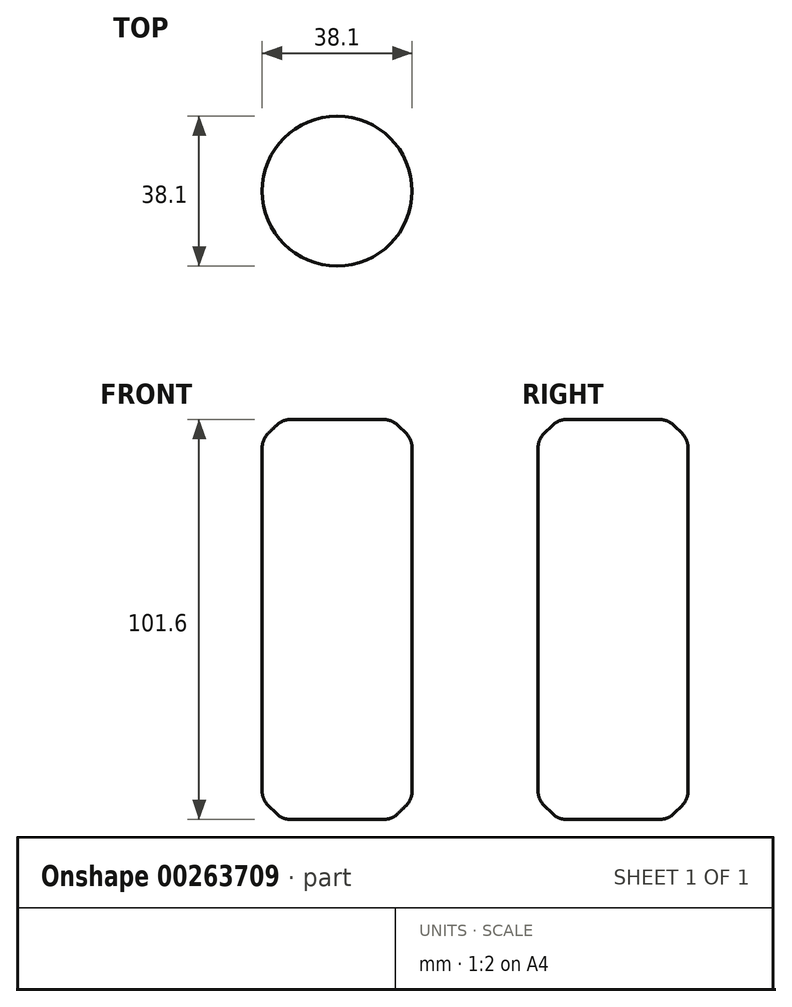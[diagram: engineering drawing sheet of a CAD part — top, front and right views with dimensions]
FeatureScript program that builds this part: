
annotation { "Feature Type Name" : "Feature", "Feature Type Description" : "" }
export const myFeature = defineFeature(function(context is Context, id is Id, definition is map)
    precondition{}
    {
        {
            var Q0;
            Q0=qCreatedBy(makeId("Top.planeOp"),FACE);
            var sketch = newSketch(context, id + "F0", { "sketchPlane" : qUnion([Q0])});
            skCircle(sketch, "E0", {"center": v(0, 0) * mm, "radius": 19.05 * mm});
            skSolve(sketch);
        }
        {
            var Q0;
            Q0=qSketchRegion(id+"F0",true);
            extrude(context, id + "F1", {"entities" : qUnion([Q0]), "depth" : 101.6 * mm});
        }
        {
            var Q0;
            Q0=makeQuery(id+"F1.opExtrude","CAP_EDGE",EDGE,{"disambiguationData":[OSD([sQuery(id+"F0.wireOp",EDGE,"E0")])],"isStart":false});
            var Q1;
            Q1=makeQuery(id+"F1.opExtrude","CAP_EDGE",EDGE,{"disambiguationData":[OSD([sQuery(id+"F0.wireOp",EDGE,"E0")])],"isStart":true});
            chamfer(context, id + "F2", {"entities" : qUnion([Q0, Q1]), "width" : 5.08 * mm, "tangentPropagation" : true});
        }
        {
            var Q0;
            Q0=makeQuery(id+"F1.opExtrude","SWEPT_FACE",FACE,{"disambiguationData":[OSD([sQuery(id+"F0.wireOp",EDGE,"E0")])]});
            var Q1;
            {var subQ0=sQuery(id+"F0.wireOp",EDGE,"E0");Q1=makeQuery(id+"F2.opChamfer","BLEND_EDGE",EDGE,{"blendedFrom":[makeQuery(id+"F1.opExtrude","CAP_EDGE",EDGE,{"disambiguationData":[OSD([subQ0])],"isStart":true}),makeQuery(id+"F1.opExtrude","CAP_FACE",FACE,{"disambiguationData":[OSD([subQ0])],"isStart":true})],"blendedInto":[makeQuery(id+"F1.opExtrude","CAP_FACE",FACE,{"disambiguationData":[OSD([subQ0])],"isStart":true})]});}
            var Q2;
            {var subQ0=sQuery(id+"F0.wireOp",EDGE,"E0");Q2=makeQuery(id+"F2.opChamfer","BLEND_EDGE",EDGE,{"blendedFrom":[makeQuery(id+"F1.opExtrude","CAP_EDGE",EDGE,{"disambiguationData":[OSD([subQ0])],"isStart":false}),makeQuery(id+"F1.opExtrude","CAP_FACE",FACE,{"disambiguationData":[OSD([subQ0])],"isStart":false})],"blendedInto":[makeQuery(id+"F1.opExtrude","CAP_FACE",FACE,{"disambiguationData":[OSD([subQ0])],"isStart":false})]});}
            fillet(context, id + "F3", {"entities" : qUnion([Q0, Q1, Q2]), "radius" : 5.08 * mm, "tangentPropagation" : true, "allowEdgeOverflow" : false});
        }
    });
